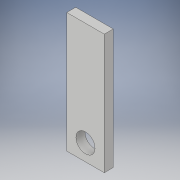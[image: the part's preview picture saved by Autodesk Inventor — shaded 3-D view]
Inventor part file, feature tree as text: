
AUTODESK INVENTOR PART (.ipt)
format: ipt  version: 2018 (Build 220112000, 112)  size: 96,256 bytes
history: native  units: in
note: dims shown in document units (in); Inventor stores cm internally (conversion verified against a paired STEP export)
features: extrude x1, sketch x1
ambient origin geometry x8: Origin, YZ Plane, XZ Plane, XY Plane, X Axis, Y Axis, Z Axis, Center Point
bodies: Solid1 (feature_tree)
feature tree (2):
  extrude  "Extrusion1"  Depth=3.1496in
  sketch  "Sketch1"  dims[d0=0.9843in d1=3.1496in d2=0.5in d3=0.2362in d4=0.0in]
